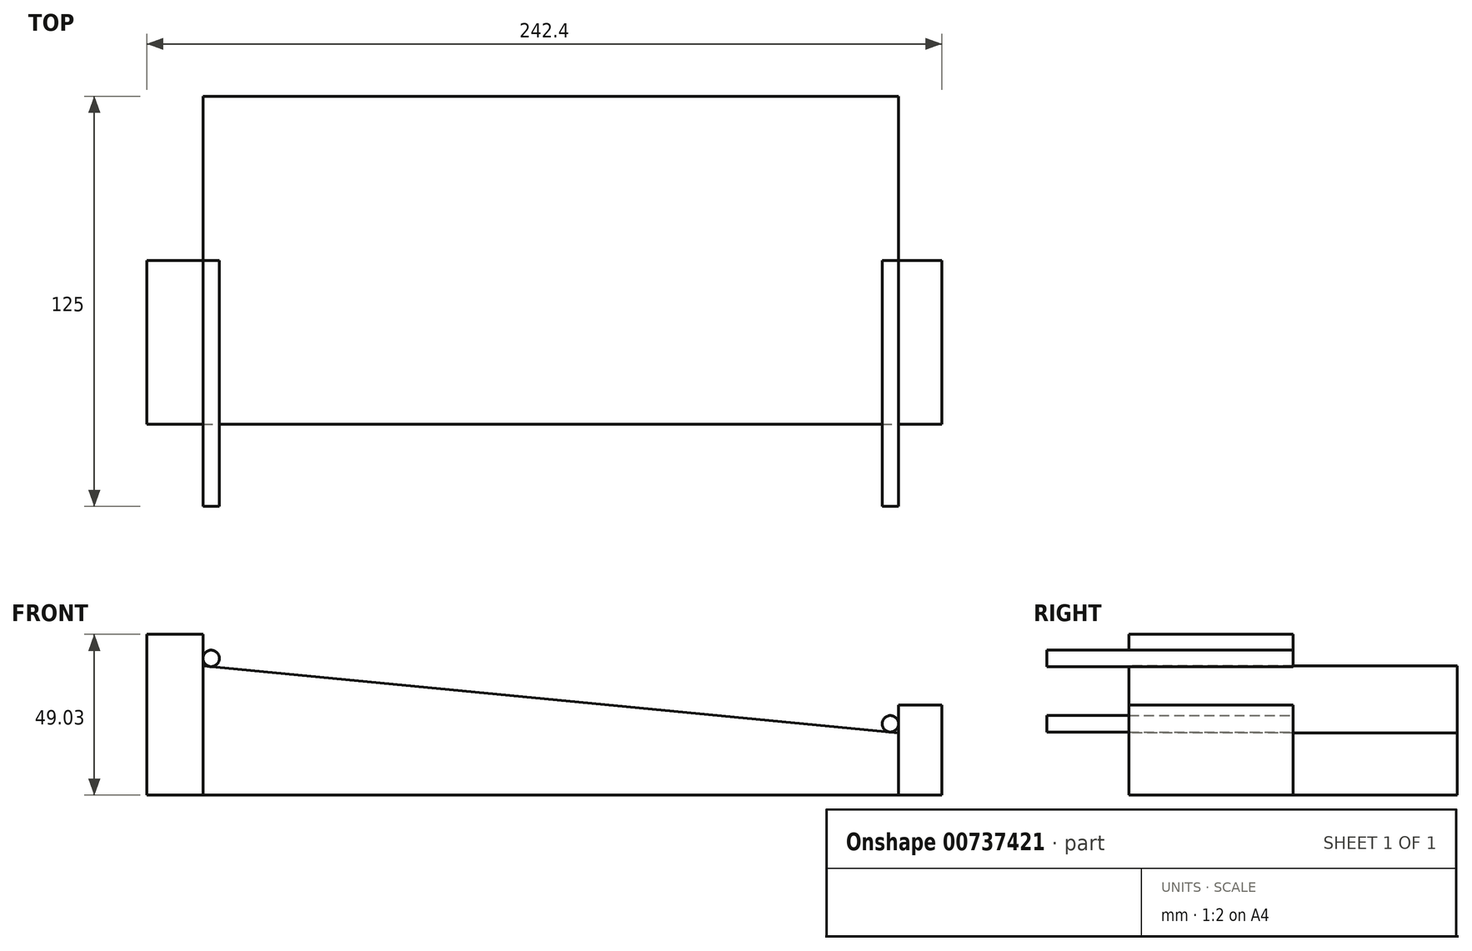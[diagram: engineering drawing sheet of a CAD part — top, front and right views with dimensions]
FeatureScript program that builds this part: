
annotation { "Feature Type Name" : "Feature", "Feature Type Description" : "" }
export const myFeature = defineFeature(function(context is Context, id is Id, definition is map)
    precondition{}
    {
        {
            var Q0;
            Q0=qCreatedBy(makeId("Front.planeOp"),FACE);
            var sketch = newSketch(context, id + "F0", { "sketchPlane" : qUnion([Q0])});
            skLineSegment(sketch, "E0", {"start": v(0, 0) * mm, "end": v(0, 39.4) * mm});
            skLineSegment(sketch, "E1", {"start": v(0, 0) * mm, "end": v(212, 0) * mm});
            skLineSegment(sketch, "E2", {"start": v(0, 39.4) * mm, "end": v(212, 18.99) * mm});
            skLineSegment(sketch, "E3", {"start": v(212, 0) * mm, "end": v(212, 18.99) * mm});
            skLineSegment(sketch, "E4", {"start": v(212, 18.99) * mm, "end": v(212, 85.03) * mm, "construction": true});
            skLineSegment(sketch, "E5", {"start": v(0, 39.4) * mm, "end": v(0, 111.14) * mm, "construction": true});
            skCircle(sketch, "E6", {"center": v(209.5, 21.74) * mm, "radius": 2.5 * mm});
            skCircle(sketch, "E7", {"center": v(2.5, 41.67) * mm, "radius": 2.5 * mm});
            skLineSegment(sketch, "E8", {"start": v(209.5, 21.74) * mm, "end": v(203.4, 21.74) * mm, "construction": true});
            skLineSegment(sketch, "E9.0", {"start": v(218, 24.24) * mm, "end": v(209.5, 24.24) * mm, "construction": true});
            skLineSegment(sketch, "E10", {"start": v(2.5, 41.67) * mm, "end": v(-3.03, 41.67) * mm, "construction": true});
            skLineSegment(sketch, "E11.0", {"start": v(2.5, 44.17) * mm, "end": v(-3.03, 44.17) * mm});
            skSolve(sketch);
        }
        {
            var Q0;
            {var subQ3=sQuery(id+"F0.wireOp",EDGE,"E0");Q0=makeQuery(id+"F0.imprint","IMPRINT",FACE,{"disambiguationData":[TD([[makeQuery(id+"F0.imprint","IMPRINT",EDGE,{"derivedFrom":subQ3}),-1.0]])]});}
            extrude(context, id + "F1", {"entities" : qUnion([Q0]), "oppositeDirection" : true, "depth" : 100 * mm, "offsetDistance" : 25 * mm});
        }
        {
            var Q0;
            Q0=makeQuery(id+"F0.imprint","IMPRINT",FACE,{"disambiguationData":[TD([[makeQuery(id+"F0.imprint","IMPRINT",EDGE,{"derivedFrom":sQuery(id+"F0.wireOp",EDGE,"E6")}),1.0]])]});
            var Q1;
            {var subQ0=sQuery(id+"F0.wireOp",EDGE,"E7");var subQ1=makeQuery(id+"F0.imprint","IMPRINT",VERTEX,{"derivedFrom":subQ0});Q1=makeQuery(id+"F0.imprint","IMPRINT",FACE,{"disambiguationData":[TD([[makeQuery(id+"F0.imprint","IMPRINT",EDGE,{"disambiguationData":[TD([[subQ1,-1.0]])],"derivedFrom":subQ0}),1.0]])]});}
            extrude(context, id + "F2", {"entities" : qUnion([Q0, Q1]), "operationType" : NewBodyOperationType.ADD, "depth" : 25 * mm, "offsetDistance" : 25 * mm, "hasSecondDirection" : true, "secondDirectionOppositeDirection" : true, "secondDirectionDepth" : 50 * mm});
        }
        {
            var Q0;
            {var subQ3=sQuery(id+"F0.wireOp",EDGE,"E0");Q0=makeQuery(id+"F0.imprint","IMPRINT",FACE,{"disambiguationData":[TD([[makeQuery(id+"F0.imprint","IMPRINT",EDGE,{"derivedFrom":subQ3}),-1.0]])]});}
            var sketch = newSketch(context, id + "F3", { "sketchPlane" : qUnion([Q0])});
            skPoint(sketch, "E12.0", {"position": v(0, 0) * mm});
            skPoint(sketch, "E13.0", {"position": v(212, 0) * mm});
            skLineSegment(sketch, "E14.bottom", {"start": v(0, 0) * mm, "end": v(-17.14, 0) * mm});
            skLineSegment(sketch, "E14.top", {"start": v(0, 49.03) * mm, "end": v(-17.14, 49.03) * mm});
            skLineSegment(sketch, "E14.left", {"start": v(0, 0) * mm, "end": v(0, 49.03) * mm});
            skLineSegment(sketch, "E14.right", {"start": v(-17.14, 0) * mm, "end": v(-17.14, 49.03) * mm});
            skLineSegment(sketch, "E15.bottom", {"start": v(212, 0) * mm, "end": v(225.26, 0) * mm});
            skLineSegment(sketch, "E15.top", {"start": v(212, 27.52) * mm, "end": v(225.26, 27.52) * mm});
            skLineSegment(sketch, "E15.left", {"start": v(212, 0) * mm, "end": v(212, 27.52) * mm});
            skLineSegment(sketch, "E15.right", {"start": v(225.26, 0) * mm, "end": v(225.26, 27.52) * mm});
            skSolve(sketch);
        }
        {
            var Q0;
            {var subQ4=sQuery(id+"F3.wireOp",EDGE,"E14.bottom");Q0=makeQuery(id+"F3.imprint","IMPRINT",FACE,{"disambiguationData":[TD([[makeQuery(id+"F3.imprint","IMPRINT",EDGE,{"derivedFrom":subQ4}),-1.0]])]});}
            var Q1;
            {var subQ4=sQuery(id+"F3.wireOp",EDGE,"E15.bottom");Q1=makeQuery(id+"F3.imprint","IMPRINT",FACE,{"disambiguationData":[TD([[makeQuery(id+"F3.imprint","IMPRINT",EDGE,{"derivedFrom":subQ4}),1.0]])]});}
            extrude(context, id + "F4", {"entities" : qUnion([Q0, Q1]), "oppositeDirection" : true, "depth" : 50 * mm, "offsetDistance" : 25 * mm});
        }
    });
